SOLIDWORKS PART (.sldprt)
format: sldprt  version: not decoded by parser v0  size: 150,528 bytes
history: native  units: mm
features: sketch x7, extrude x2, hole x2, material x1, cut_extrude x1, pattern_circular x1 (+12 scaffold rows collapsed)
feature tree (26):
  scaffold x12  (default folders/planes/origin — collapsed)
  material  "Material <not specified>"
  sketch  "Sketch1"
  extrude  "Boss-Extrude1"  Depth=7mm
  sketch  "Sketch2"  dims[D1=40.0mm D2=10.0mm D3=10.0mm]
  extrude  "Boss-Extrude2"  Depth=7mm
  hole  "CSK for M6 Countersunk Flat Head Screw2"  Diameter=6.6mm Depth=7mm
  sketch  "Sketch7"
  sketch  "Sketch6"  dims[hole-wizard template sketch: 55 standard entries collapsed; hole parameters kept: c17.Thru Hole Depth=7.0mm c17.Near C'Sink Dia.=12.6mm c17.D4=~3.666174mm c17.Near C'Sink Angle=90.0deg]
  sketch  "Sketch10"
  cut_extrude  "Cut-Extrude1"  Depth=3mm
  hole  "M4 Clearance Hole1"  Diameter=4.5mm Depth=10mm
  sketch  "Sketch12"
  sketch  "Sketch11"  dims[hole-wizard template sketch: 47 standard entries collapsed; hole parameters kept: c15.Hole Depth=10.0mm c15.D3=~14.816244mm c15.Drill Angle=118.0deg]
  pattern_circular  "CirPattern1"  Count=2 Angle=360deg
decode coverage: 9 of 13 modeling features carry decoded parameters
note: ~ marks probable driven/reference dimensions
note: suppression state not decoded; provenance and decode notes live in map.json
